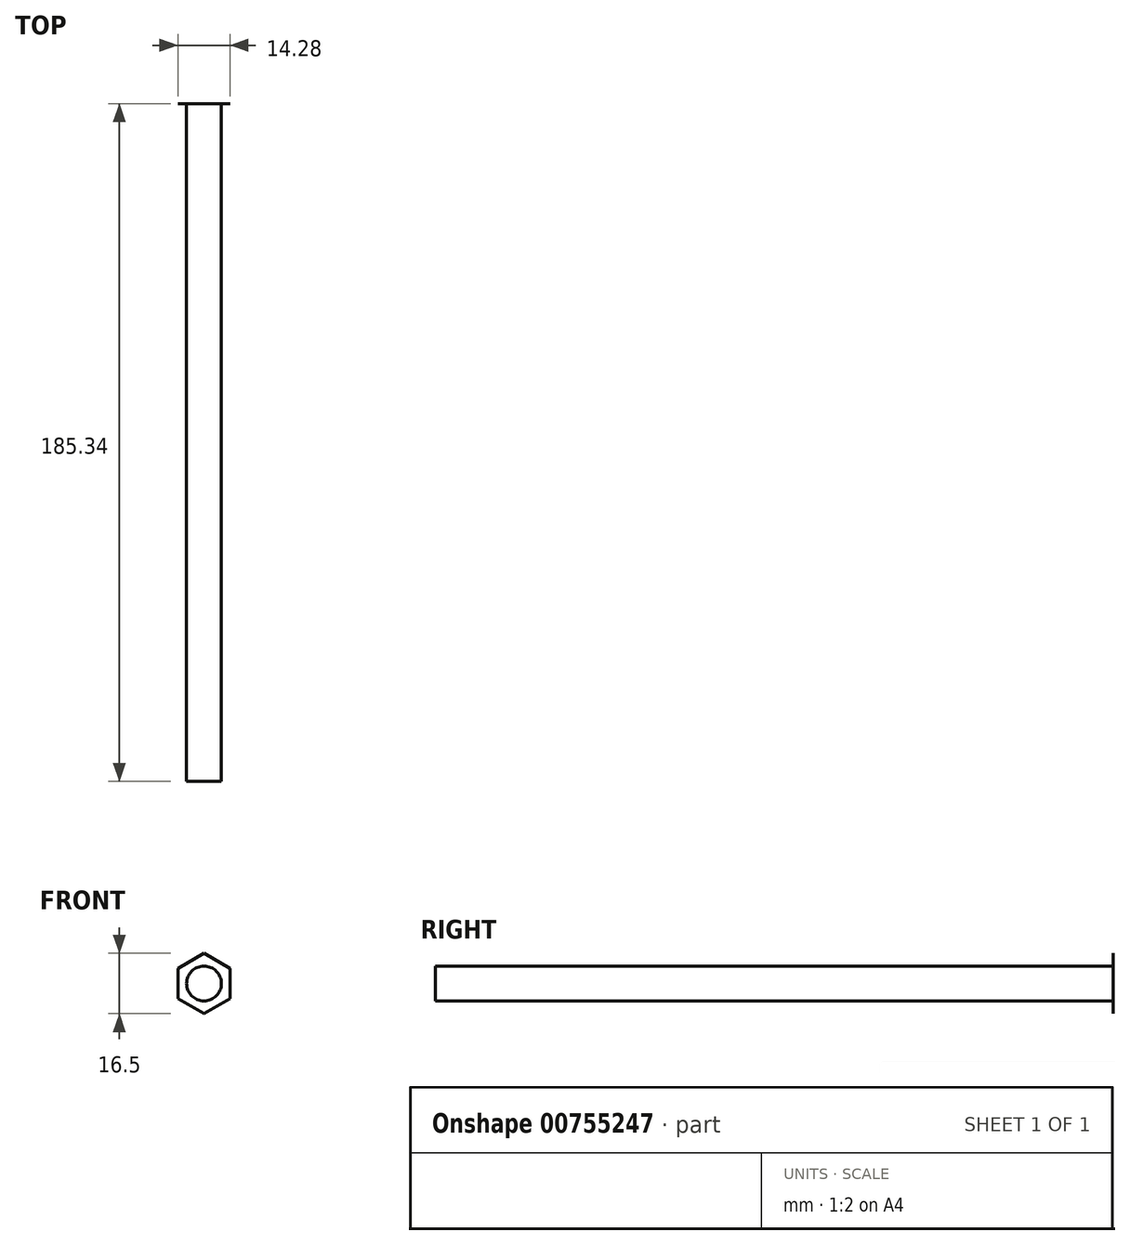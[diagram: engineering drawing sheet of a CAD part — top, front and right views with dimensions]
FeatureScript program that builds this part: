
annotation { "Feature Type Name" : "Feature", "Feature Type Description" : "" }
export const myFeature = defineFeature(function(context is Context, id is Id, definition is map)
    precondition{}
    {
        {
            var Q0;
            Q0=qCreatedBy(makeId("Front.planeOp"),FACE);
            var sketch = newSketch(context, id + "F0", { "sketchPlane" : qUnion([Q0])});
            skCircle(sketch, "E0.cCircle", {"center": v(0, 0) * mm, "radius": 7.14 * mm, "construction": true});
            skLineSegment(sketch, "E0.0", {"start": v(7.14, 4.12) * mm, "end": v(7.14, -4.12) * mm});
            skLineSegment(sketch, "E0.1", {"start": v(7.14, -4.12) * mm, "end": v(0, -8.25) * mm});
            skLineSegment(sketch, "E0.2", {"start": v(0, -8.25) * mm, "end": v(-7.14, -4.12) * mm});
            skLineSegment(sketch, "E0.3", {"start": v(-7.14, -4.12) * mm, "end": v(-7.14, 4.12) * mm});
            skLineSegment(sketch, "E0.4", {"start": v(-7.14, 4.12) * mm, "end": v(0, 8.25) * mm});
            skLineSegment(sketch, "E0.5", {"start": v(0, 8.25) * mm, "end": v(7.14, 4.12) * mm});
            skPoint(sketch, "E0.0.midPoint", {"position": v(7.14, 0) * mm});
            skCircle(sketch, "E1", {"center": v(0, 0) * mm, "radius": 4.76 * mm});
            skSolve(sketch);
        }
        {
            var Q0;
            Q0=makeQuery(id+"F0.imprint","IMPRINT",FACE,{"disambiguationData":[TD([[makeQuery(id+"F0.imprint","IMPRINT",EDGE,{"derivedFrom":sQuery(id+"F0.wireOp",EDGE,"E1")}),1.0]])]});
            var Q1;
            Q1=sQuery(id+"F0.wireOp",EDGE,"E1");
            extrude(context, id + "F1", {"entities" : qUnion([Q0]), "surfaceEntities" : qUnion([Q1]), "depth" : 185.34 * mm, "offsetDistance" : 25.4 * mm});
        }
        {
            var Q0;
            Q0 = qSketchRegion(id + "F0", true);
            extrude(context, id + "F2", {"entities" : qUnion([Q0]), "operationType" : NewBodyOperationType.ADD, "depth" : 15 / 1701.8 * mm, "offsetDistance" : 25.4 * mm});
        }
    });
